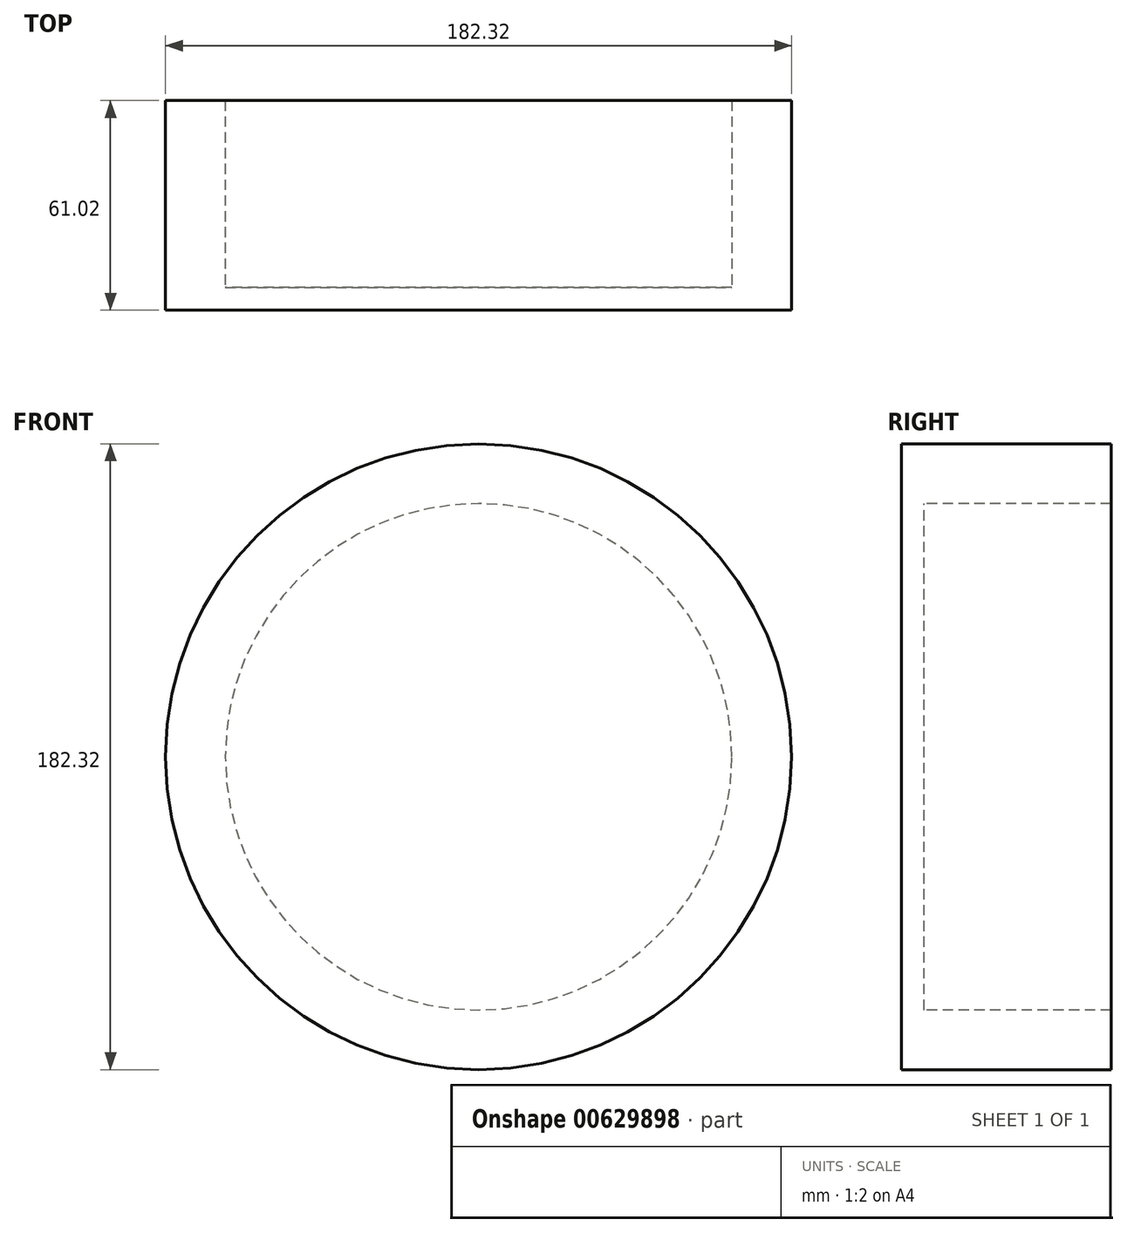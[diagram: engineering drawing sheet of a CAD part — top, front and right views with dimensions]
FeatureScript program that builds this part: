
annotation { "Feature Type Name" : "Feature", "Feature Type Description" : "" }
export const myFeature = defineFeature(function(context is Context, id is Id, definition is map)
    precondition{}
    {
        {
            var Q0;
            Q0=qCreatedBy(makeId("Top.planeOp"),FACE);
            var sketch = newSketch(context, id + "F0", { "sketchPlane" : qUnion([Q0])});
            skLineSegment(sketch, "E0", {"start": v(-43, 0) * mm, "end": v(30.75, 0) * mm});
            skLineSegment(sketch, "E1", {"start": v(30.75, 0) * mm, "end": v(30.75, 54.4) * mm});
            skLineSegment(sketch, "E2", {"start": v(30.75, 54.4) * mm, "end": v(48.15, 54.4) * mm});
            skLineSegment(sketch, "E3", {"start": v(48.15, 54.4) * mm, "end": v(48.15, -6.62) * mm});
            skLineSegment(sketch, "E4", {"start": v(48.15, -6.62) * mm, "end": v(-43, -6.62) * mm});
            skLineSegment(sketch, "E5", {"start": v(-43, -6.62) * mm, "end": v(-43, 0) * mm});
            skLineSegment(sketch, "E6", {"start": v(-43, 0) * mm, "end": v(-43, 54.4) * mm});
            skSolve(sketch);
        }
        {
            var Q0;
            Q0=makeQuery(id+"F0.imprint","IMPRINT",FACE,{"disambiguationData":[TD([[makeQuery(id+"F0.imprint","IMPRINT",EDGE,{"derivedFrom":sQuery(id+"F0.wireOp",EDGE,"E0")}),-1.0]])]});
            var Q1;
            Q1=sQuery(id+"F0.wireOp",EDGE,"E6");
            revolve(context, id + "F1", {"entities" : qUnion([Q0]), "axis" : qUnion([Q1]), "revolveType" : RevolveType.FULL});
        }
    });
